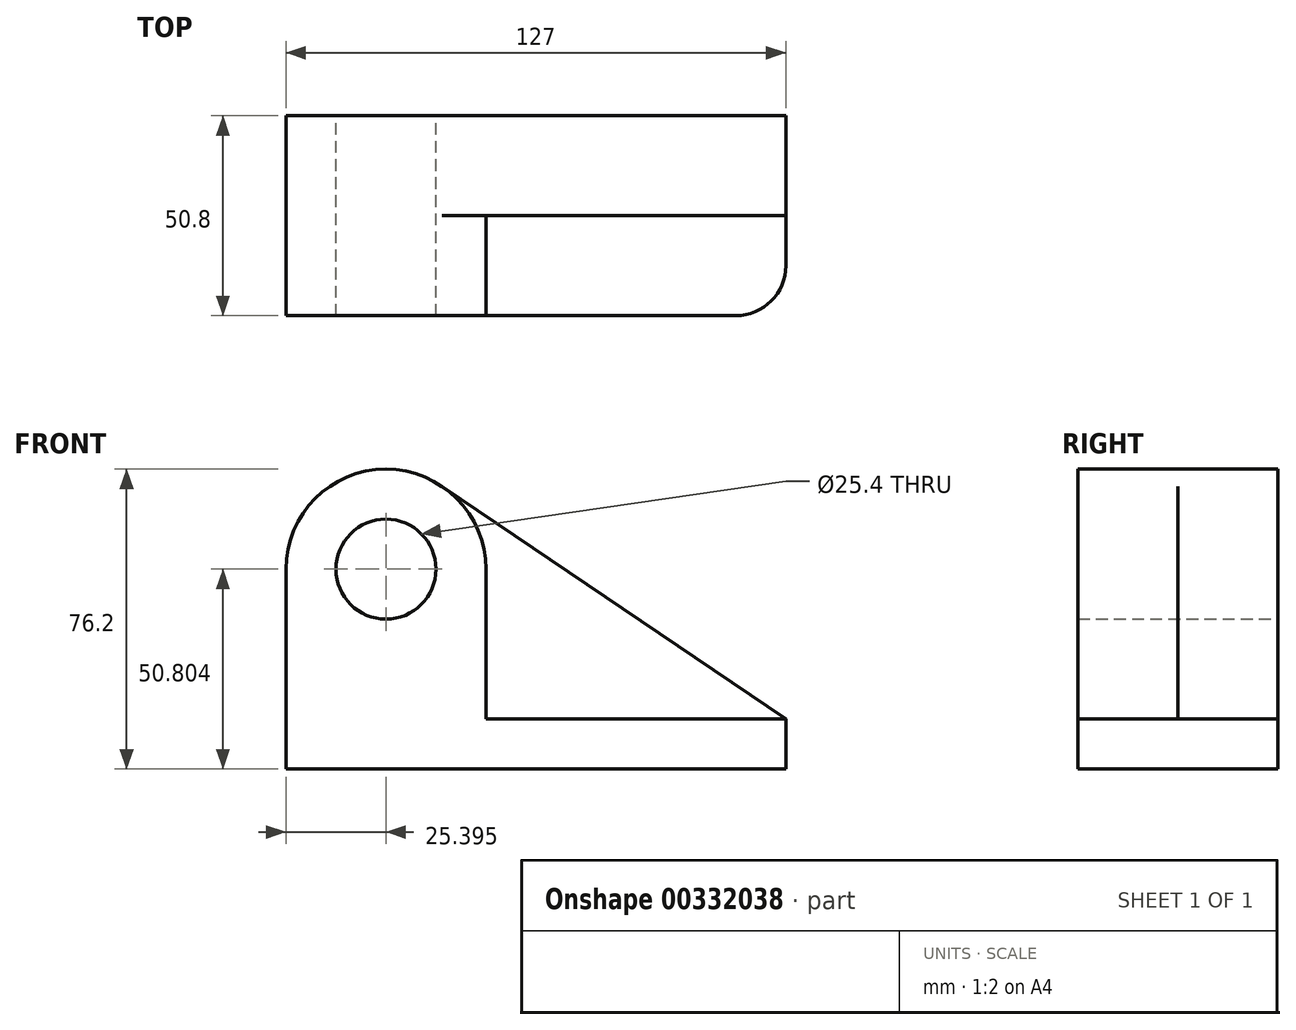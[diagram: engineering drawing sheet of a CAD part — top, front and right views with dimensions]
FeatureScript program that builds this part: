
annotation { "Feature Type Name" : "Feature", "Feature Type Description" : "" }
export const myFeature = defineFeature(function(context is Context, id is Id, definition is map)
    precondition{}
    {
        {
            var Q0;
            Q0=qCreatedBy(makeId("Front.planeOp"),FACE);
            var sketch = newSketch(context, id + "F0", { "sketchPlane" : qUnion([Q0])});
            skCircle(sketch, "E0", {"center": v(-46.88, 40.5) * mm, "radius": 12.7 * mm});
            skArc(sketch, "E1", {"start": v(-32.65, 61.53) * mm, "mid": v(-58.8, 62.93) * mm, "end": v(-72.28, 40.5) * mm});
            skLineSegment(sketch, "E2", {"start": v(-72.28, 40.5) * mm, "end": v(-72.28, -10.3) * mm});
            skLineSegment(sketch, "E3", {"start": v(-72.28, -10.3) * mm, "end": v(54.72, -10.3) * mm});
            skLineSegment(sketch, "E4", {"start": v(54.72, -10.3) * mm, "end": v(54.72, 2.4) * mm});
            skLineSegment(sketch, "E5", {"start": v(54.72, 2.4) * mm, "end": v(-32.65, 61.53) * mm});
            skSolve(sketch);
        }
        {
            var Q0;
            Q0=makeQuery(id+"F0.imprint","IMPRINT",FACE,{"disambiguationData":[TD([[makeQuery(id+"F0.imprint","IMPRINT",EDGE,{"derivedFrom":sQuery(id+"F0.wireOp",EDGE,"E0")}),-1.0]])]});
            extrude(context, id + "F1", {"entities" : qUnion([Q0]), "depth" : 25.4 * mm});
        }
        {
            var Q0;
            Q0=makeQuery(id+"F1.opExtrude","CAP_FACE",FACE,{"disambiguationData":[OSD([sQuery(id+"F0.wireOp",EDGE,"E0"),sQuery(id+"F0.wireOp",EDGE,"E1"),sQuery(id+"F0.wireOp",EDGE,"E2"),sQuery(id+"F0.wireOp",EDGE,"E3"),sQuery(id+"F0.wireOp",EDGE,"E4"),sQuery(id+"F0.wireOp",EDGE,"E5")])],"isStart":false});
            var sketch = newSketch(context, id + "F2", { "sketchPlane" : qUnion([Q0])});
            skCircle(sketch, "E6", {"center": v(-46.88, 40.5) * mm, "radius": 12.7 * mm});
            skCircle(sketch, "E7", {"center": v(-46.88, 40.5) * mm, "radius": 25.4 * mm});
            skLineSegment(sketch, "E8", {"start": v(54.72, 2.4) * mm, "end": v(-72.28, 2.4) * mm});
            skLineSegment(sketch, "E9", {"start": v(-21.48, 40.5) * mm, "end": v(-21.48, 2.4) * mm});
            skLineSegment(sketch, "E10", {"start": v(-72.28, 40.5) * mm, "end": v(-72.28, 2.4) * mm});
            skSolve(sketch);
        }
        {
            var Q0;
            Q0 = qSketchRegion(id + "F2", true);
            var Q1;
            {var subQ0=makeQuery(id+"F1.opExtrude","CAP_EDGE",EDGE,{"disambiguationData":[OSD([sQuery(id+"F0.wireOp",EDGE,"E3")])],"isStart":false});Q1=makeQuery(id+"F2.imprint","IMPRINT",FACE,{"disambiguationData":[TD([[makeQuery(id+"F2.imprint","IMPRINT",EDGE,{"derivedFrom":subQ0}),1.0]])]});}
            extrude(context, id + "F3", {"entities" : qUnion([Q0, Q1]), "operationType" : NewBodyOperationType.ADD, "depth" : 25.4 * mm});
        }
        {
            var Q0;
            Q0=makeQuery(id+"F3.opExtrude","CAP_EDGE",EDGE,{"disambiguationData":[OSD([sQuery(id+"F0.wireOp",EDGE,"E4")])],"isStart":false});
            fillet(context, id + "F4", {"entities" : qUnion([Q0]), "radius" : 12.7 * mm, "tangentPropagation" : true, "allowEdgeOverflow" : false});
        }
    });
